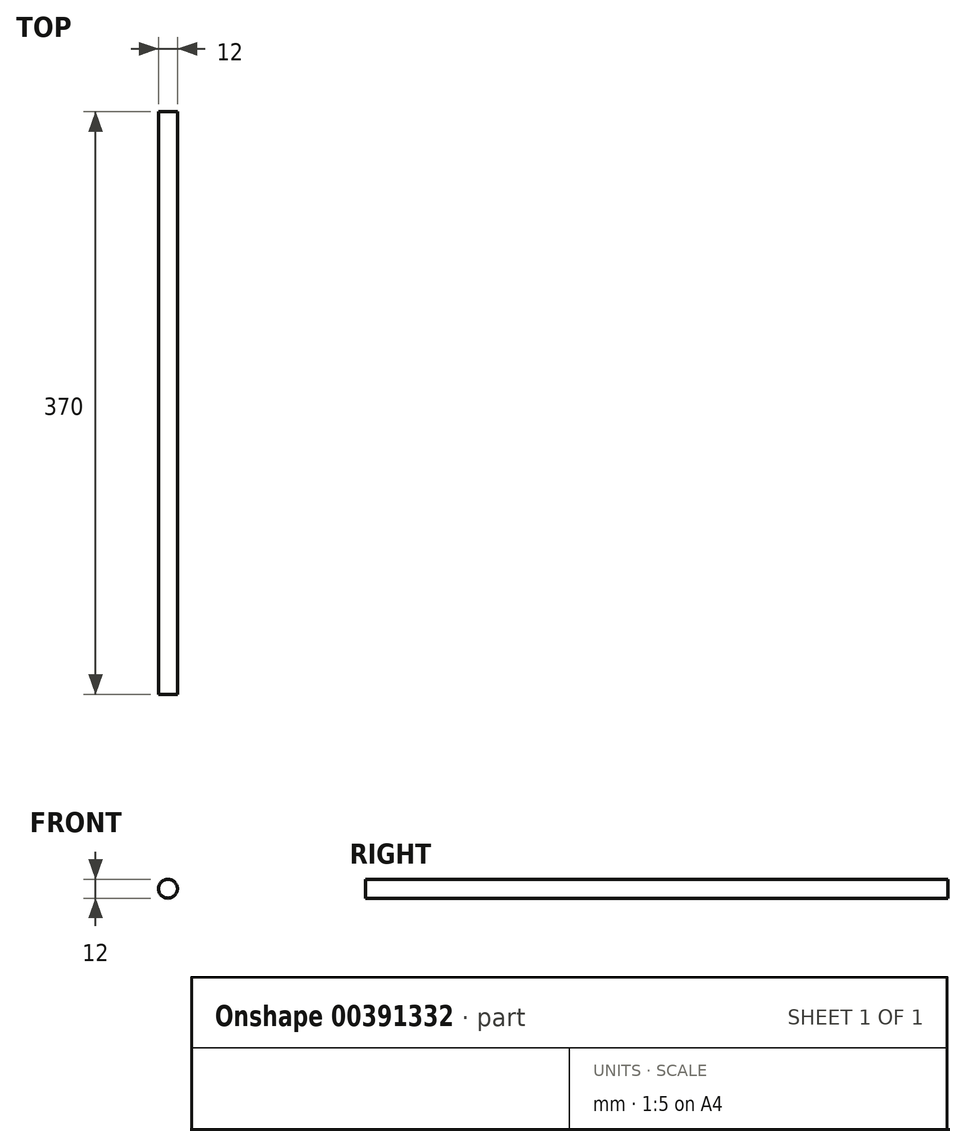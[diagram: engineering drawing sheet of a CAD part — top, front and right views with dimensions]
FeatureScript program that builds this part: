
annotation { "Feature Type Name" : "Feature", "Feature Type Description" : "" }
export const myFeature = defineFeature(function(context is Context, id is Id, definition is map)
    precondition{}
    {
        {
            var Q0;
            Q0=qCreatedBy(makeId("Front.planeOp"),FACE);
            var sketch = newSketch(context, id + "F0", { "sketchPlane" : qUnion([Q0])});
            skCircle(sketch, "E0", {"center": v(0, 0) * mm, "radius": 6 * mm});
            skSolve(sketch);
        }
        {
            var Q0;
            Q0=makeQuery(id+"F0.imprint","IMPRINT",FACE,{"disambiguationData":[TD([[makeQuery(id+"F0.imprint","IMPRINT",EDGE,{"derivedFrom":sQuery(id+"F0.wireOp",EDGE,"E0")}),1.0]])]});
            extrude(context, id + "F1", {"entities" : qUnion([Q0]), "endBound" : BoundingType.SYMMETRIC, "depth" : 370 * mm});
        }
    });
